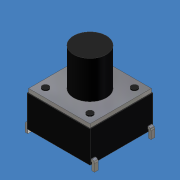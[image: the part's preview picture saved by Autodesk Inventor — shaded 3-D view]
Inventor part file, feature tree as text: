
AUTODESK INVENTOR PART (.ipt)
format: ipt  version: unknown  size: 240,640 bytes
history: native  units: mm (DEFAULTED — no unit token found)
features: sketch x6, extrude x4, mirror x2, pattern_circular x1, plane x1, sweep x1
ambient origin geometry x8: Origin, YZ Plane, XZ Plane, XY Plane, X Axis, Y Axis, Z Axis, Center Point
feature tree (15):
  extrude  "Extrusion1"  Depth=3.175mm TaperAngle=0.0deg
  extrude  "Extrusion2"  Depth=4.1656mm TaperAngle=0.0deg
  extrude  "Extrusion3"  Depth=0.508mm TaperAngle=0.0deg
  pattern_circular  "Circular Pattern1"  Count=4 Angle=360.0deg
  extrude  "Extrusion4"  Depth=0.381mm
  sketch  "Sketch5"  dims[d15=0.254mm d16=0.127mm]
  plane  "Work Plane1"
  sweep  "Sweep1"
  mirror  "Mirror1"
  mirror  "Mirror2"
  sketch  "Sketch1"  dims[d0=6.35mm d1=3.175mm d2=0.0mm]
  sketch  "Sketch2"  dims[d3=3.302mm d4=4.1656mm d5=0.0mm]
  sketch  "Sketch3"  dims[d6=0.635mm d7=0.508mm d8=0.0mm d9=40.0mm d11=360.0deg]
  sketch  "Sketch4"  dims[d12=0.381mm d13=0.0mm d14=0.381mm]
  sketch  "Sketch6"  dims[d17=0.254mm d18=90.0deg d19=0.508mm d20=1.016mm d21=0.254mm d22=0.0mm]
